# Revit family: Comfort_Window_E_Side_Hung_Standard
name_source: partatom
category: Windows
revit_build: Autodesk Revit 2014 (Build: 20130308_1515(x64)
units: mm (PartAtom-declared; Revit-internal decimal feet)

## types (6) — shared parameters
DG Gasket Thickness = 12 mm  [stored 0.0393701 ft]
Description = Comfort Window, Side Hung, Type E
Double Glazing Gasket Finish = Double Glazing Gasket Material
Frame Depth = 33 mm  [stored 0.108268 ft]
Frame Edge Thickness = 26 mm
Limit Fixed Pane Height Max = 1800 mm  [stored 5.90551 ft]
Limit Fixed Pane Height Min = 200 mm  [stored 0.656168 ft]
Limit Fixed Pane Width Max = 1800 mm  [stored 5.90551 ft]
Limit Fixed Pane Width Min = 200 mm  [stored 0.656168 ft]
Limit Sash Height Max = 1200 mm
Limit Sash Height Min = 300 mm  [stored 0.984252 ft]
Limit Sash Width Max = 600 mm  [stored 1.9685 ft]
Limit Sash Width Min = 300 mm  [stored 0.984252 ft]
Limit Window Height Max = 1852 mm
Manufacturer = Crealco
Max System DG One Piece Thickness = 4 mm  [stored 0.0131234 ft]
Max System DG Unit Thickness = 20 mm  [stored 0.0656168 ft]
Model = Comfort Window
Mullion Width = 27 mm  [stored 0.0885827 ft]
Rough Height = 590 mm  [stored 1.9357 ft]
Rough Width = 902 mm  [stored 2.95932 ft]
Sash Frame Gap = 5 mm  [stored 0.0164042 ft]
Sash Frame Side Gap = 12 mm  [stored 0.0393701 ft]
Sash Side Gap = 38 mm
Set Sash Height = 1115 mm  [stored 3.65814 ft]
Set Sash Width = 515 mm  [stored 1.68963 ft]
Transom Height = 27 mm  [stored 0.0885827 ft]
URL = http://www.crealco.co.za
zero-valued in all types: Visual Light Transmittance

## per-type parameters (varying)
| type | Clearvue SHGC Value | Clearvue U Value | Energy Advantage SHGC Value | Energy Advantage U Value | Intruderprufe LowE SHGC Value | Intruderprufe LowE U Value | Intruderprufe SHGC Value | Intruderprufe U Value | SmartGlass Elite SHGC Value | SmartGlass Elite U Value | SmartGlass Plus SHGC Value | SmartGlass Plus U Value | SmartGlass Standard SHGC Value | SmartGlass Standard U Value | SmartGlass Superior SHGC Value | SmartGlass Superior U Value | Window Height | Window Width |
| Comfort-0915S | 0.574 | 6.12 | 0.516 | 4.77 | 0.49 | 4.64 | 0.548 | 6.01 | 0.283 | 3.49 | 0.384 | 3.63 | 0.514 | 4.12 | 0.247 | 3.5 | 1490 mm  [stored 4.88845 ft] | 890 mm  [stored 2.91995 ft] |
| Comfort-1215S | 0.631 | 6.07 | 0.565 | 4.55 | 0.534 | 4.43 | 0.599 | 5.96 | 0.307 | 3.11 | 0.418 | 3.27 | 0.562 | 3.84 | 0.267 | 3.12 | 1490 mm  [stored 4.88845 ft] | 1190 mm  [stored 3.9042 ft] |
| Comfort-1515S | 0.664 | 6.04 | 0.595 | 4.42 | 0.56 | 4.31 | 0.63 | 5.93 | 0.321 | 2.89 | 0.439 | 3.06 | 0.59 | 3.67 | 0.279 | 2.9 | 1490 mm  [stored 4.88845 ft] | 1490 mm  [stored 4.88845 ft] |
| Comfort-0918S | 0.593 | 6.1 | 0.532 | 4.7 | 0.504 | 4.58 | 0.565 | 6 | 0.291 | 3.38 | 0.395 | 3.52 | 0.53 | 4.03 | 0.254 | 3.38 | 1790 mm  [stored 5.8727 ft] | 890 mm  [stored 2.91995 ft] |
| Comfort-1218S | 0.647 | 6.05 | 0.58 | 4.49 | 0.547 | 4.38 | 0.614 | 5.95 | 0.314 | 3.01 | 0.428 | 3.18 | 0.575 | 3.76 | 0.273 | 3.02 | 1790 mm  [stored 5.8727 ft] | 1190 mm  [stored 3.9042 ft] |
| Comfort-1518S | 0.679 | 6.02 | 0.608 | 4.37 | 0.572 | 4.26 | 0.644 | 5.91 | 0.327 | 2.8 | 0.447 | 2.97 | 0.603 | 3.6 | 0.284 | 2.8 | 1790 mm  [stored 5.8727 ft] | 1490 mm  [stored 4.88845 ft] |

note: [stored X ft] marks values corroborated as IEEE doubles in the binary element streams (Revit-internal decimal feet)

## geometry (parser evidence)
native form markers: Sweep x18
no freeform markers — native parametric forms only
